# Revit family: Sink-Kitchen-Sterling-Middleton-14631
name_source: partatom
category: Plumbing Fixtures
revit_build: Autodesk Revit 2015 (Build: 20140606_1530(x64)
units: mm (PartAtom-declared; Revit-internal decimal feet)

## types (4) — shared parameters
ADA Compliant = Yes
Assembly Code = D2010400
Date Modified = 04/06/2018
Default Elevation = 36"
Description = Middleton Single-basin Kitchen Sink, 25inch x 22inch
Finish = Metal-Kohler-NA-Stainless
Height = 6 1/4"
Inlet Connection = Inlet Connection
Length = 25"
Manufacturer = Sterling
MasterFormat 1995 = 15410
MasterFormat 2004 = 22.41.16
Material = 20 gauge stainless steel
Outlet Connection = Outlet Connection
Product Name = Middleton
Product Page URL = http://www.sterlingplumbing.com
URL = https://www.sterlingplumbing.com
Waste Connection = Yes
Width = 22"

## per-type parameters (varying)
| type | Hand Spray | Model | Product Documentation Link | Type |
| Three Faucet Holes-NA-Stainless | No | 14631-3-NA | https://www.sterlingplumbing.com | 1 |
| Four Faucet Holes-NA-Stainless | Yes | 14631-4-NA | https://resources.kohler.com | 2 |
| 50 Per Pack-Three Faucet Holes-NA-Stainless | No | K-14631-3F-NA | https://www.sterlingplumbing.com | 3 |
| 50 Per Pack-Four Faucet Holes-NA-Stainless | Yes | 14631-4F-NA | https://resources.kohler.com | 4 |

## geometry (parser evidence)
native form markers: Blend x4, Sweep x7
no freeform markers — native parametric forms only
